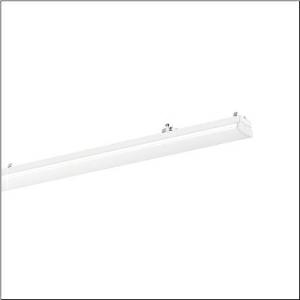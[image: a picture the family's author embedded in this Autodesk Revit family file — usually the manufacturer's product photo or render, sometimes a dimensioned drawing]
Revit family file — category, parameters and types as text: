
# Revit family: licross_r__11_recessed_opal_mo_51te1dcn485g_f99d
name_source: partatom
category: Lighting Fixtures
units: mm (PartAtom-declared; Revit-internal decimal feet)

## family parameters
Cut with Voids When Loaded = No
Host = Face
Light Source = No
Part Type = Normal
Room Calculation Point = No
Round Connector Dimension = Use Diameter
Shared = No

## types (1)
- --- (1 x LED, 8820 lm, 49.3 W, 4000K)
    Apparent Load = 49 VA
    CIE Flux Codes = 44 73 91 87 100
    Color Rendering = 80
    Color Temperature = 4000K
    Default Elevation = 1800 mm
    Description = Licross® 11 recessed opal MO, luminaire insert, of sheet steel, coil coated, white, length: 1.500mm, width: 76mm, height: 87mm, LED rated luminous flux: 8.820lm, light colour: 840, control gear: ON/OFF Multilumen, CLOi, with plug, 3-pole, with phase selection, mains connection: 220..240V, AC, 50/60Hz, start of lifetime: 49W, end of service life: 55W, internal wiring halogen-free, primary optical cover: cover, of PMMA, light emission: direct with ceiling illumination distribution, primary light characteristic: symmetric, protection rating (complete): IP54, insulation class (complete): insulation class I (protective earthing), certification: CE, ENEC, VDE, UKCA, protection symbol: D if used in an environment with non-conductive dust loads with corresponding accessories, impact resistance: IK06, permissible ambient temperature for indoor applications: -35..+40°C, corresponds to IFS (International Featured Standards) requirements for safety and quality in the food industry, reducing of maximum allowable ambient temperature of 5°C with ceiling mounting, LABS conformity tested according to VDMA 24364:2018-05, packaging unit: 1 piece
    Height = 83 mm
    Lamp = 1 x LED
    Lamp Light Flux = 8820 lm
    Lamp Power = 49.3 W
    Lamp count = 1
    Length = 1500 mm
    Luminous efficacy = 179 lm/W
    Manufacturer = Siteco
    ModVariant = No
    Model = 51TE1DCN485G
    Mounting Place = Ceiling
    Mounting Type = Pendant
    Number of Poles = 1
    OnlyDefault = Yes
    Power Factor = 1
    Product Name = Licross® 11 recessed opal MO
    Product group = luminaire insert | ceiling pendant
    ProductGroupID = 902
    Protection Class = Protection class I
    Protection Degree = IP 54
    RLX_Detail_Level = 1
    RLX_Emergency_Light_Flux = 0 lm
    RLX_Emergency_Type = 0
    RLX_Emergency_Type_DB = No
    RlxData = <blob elided: 24877 chars, md5=5e237238>
    Socket = socket
    Standby Power = 0 W
    System Light Flux = 8820 lm
    System Power = 49 W
    Type Comments = factory setting: luminous flux: 100 % | (A | C | E) | 113 mA
    Type Image = l_1313666.jpg
    URL = http://relux.com
    VarID = @adj_089861
    Voltage = 0 V
    Weight = 0.00 kg
    Width = 76 mm

## geometry (parser evidence)
native form markers: Blend x4, Sweep x13
no freeform markers — native parametric forms only
